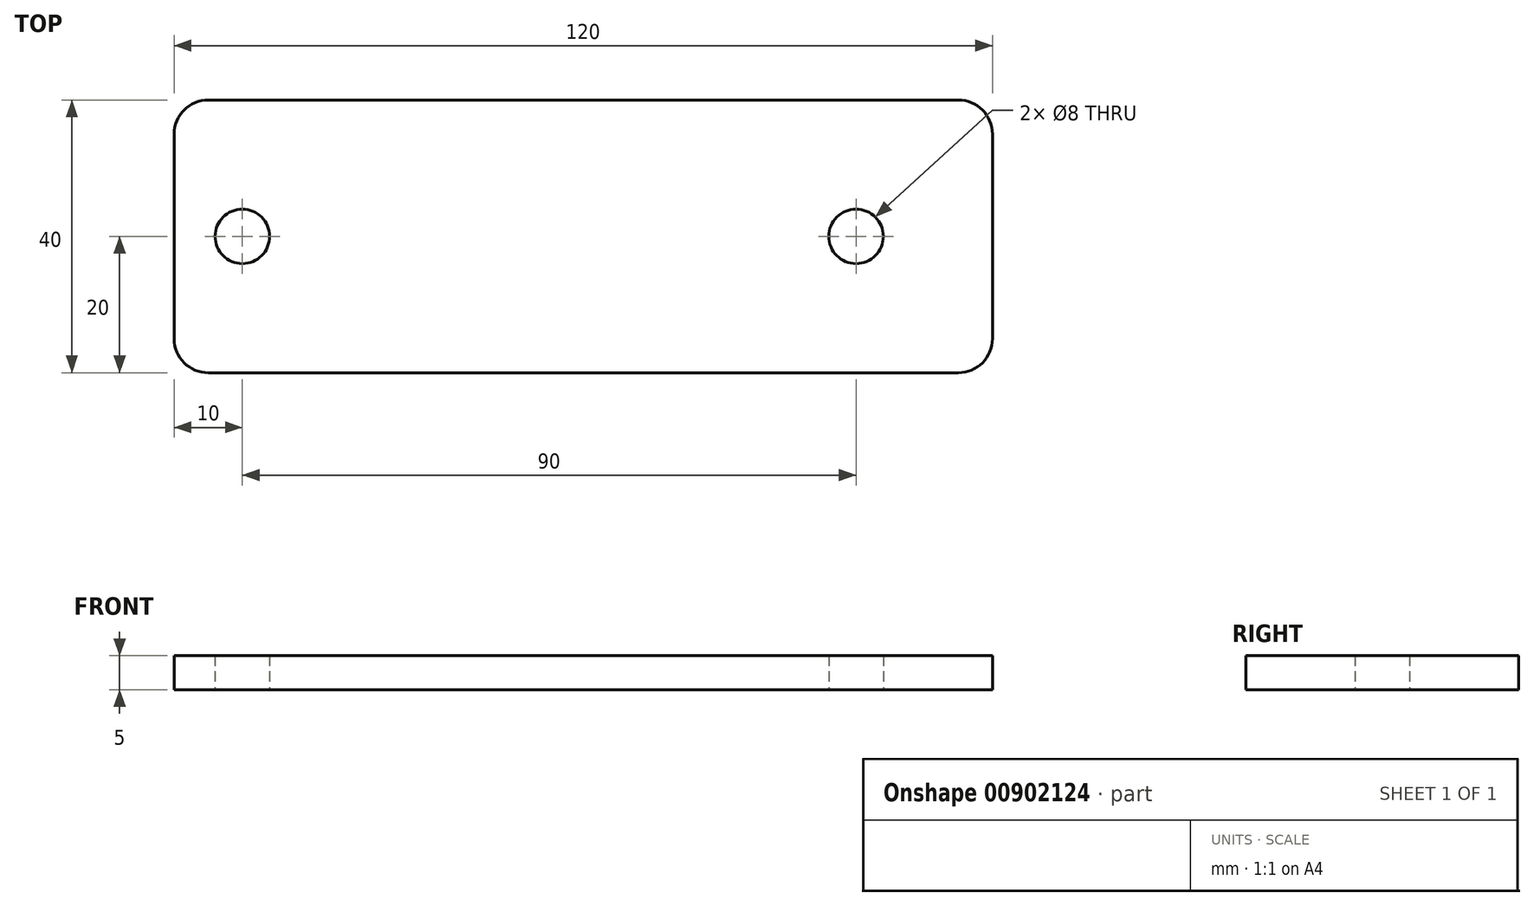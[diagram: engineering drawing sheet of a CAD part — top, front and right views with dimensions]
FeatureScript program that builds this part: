
annotation { "Feature Type Name" : "Feature", "Feature Type Description" : "" }
export const myFeature = defineFeature(function(context is Context, id is Id, definition is map)
    precondition{}
    {
        {
            var Q0;
            Q0=qCreatedBy(makeId("Top.planeOp"),FACE);
            var sketch = newSketch(context, id + "F0", { "sketchPlane" : qUnion([Q0])});
            skLineSegment(sketch, "E0.bottom", {"start": v(0, 0) * mm, "end": v(-120, 0) * mm});
            skLineSegment(sketch, "E0.top", {"start": v(0, 40) * mm, "end": v(-120, 40) * mm});
            skLineSegment(sketch, "E0.left", {"start": v(0, 0) * mm, "end": v(0, 40) * mm});
            skLineSegment(sketch, "E0.right", {"start": v(-120, 0) * mm, "end": v(-120, 40) * mm});
            skCircle(sketch, "E1", {"center": v(-110, 20) * mm, "radius": 4 * mm});
            skCircle(sketch, "E2", {"center": v(-20, 20) * mm, "radius": 4 * mm});
            skSolve(sketch);
        }
        {
            var Q0;
            Q0=makeQuery(id+"F0.imprint","IMPRINT",FACE,{"disambiguationData":[TD([[makeQuery(id+"F0.imprint","IMPRINT",EDGE,{"derivedFrom":sQuery(id+"F0.wireOp",EDGE,"E0.bottom")}),-1.0]])]});
            extrude(context, id + "F1", {"entities" : qUnion([Q0]), "depth" : 5 * mm, "offsetDistance" : 25 * mm});
        }
        {
            var Q0;
            Q0=makeQuery(id+"F1.opExtrude","SWEPT_EDGE",EDGE,{"disambiguationData":[OSD([sQuery(id+"F0.wireOp",EDGE,"E0.top"),sQuery(id+"F0.wireOp",EDGE,"E0.left")])]});
            var Q1;
            Q1=makeQuery(id+"F1.opExtrude","SWEPT_EDGE",EDGE,{"disambiguationData":[OSD([sQuery(id+"F0.wireOp",EDGE,"E0.bottom"),sQuery(id+"F0.wireOp",EDGE,"E0.left")])]});
            var Q2;
            Q2=makeQuery(id+"F1.opExtrude","SWEPT_EDGE",EDGE,{"disambiguationData":[OSD([sQuery(id+"F0.wireOp",EDGE,"E0.bottom"),sQuery(id+"F0.wireOp",EDGE,"E0.right")])]});
            var Q3;
            Q3=makeQuery(id+"F1.opExtrude","SWEPT_EDGE",EDGE,{"disambiguationData":[OSD([sQuery(id+"F0.wireOp",EDGE,"E0.top"),sQuery(id+"F0.wireOp",EDGE,"E0.right")])]});
            fillet(context, id + "F2", {"entities" : qUnion([Q0, Q1, Q2, Q3]), "radius" : 5 * mm, "tangentPropagation" : true, "allowEdgeOverflow" : false});
        }
    });
